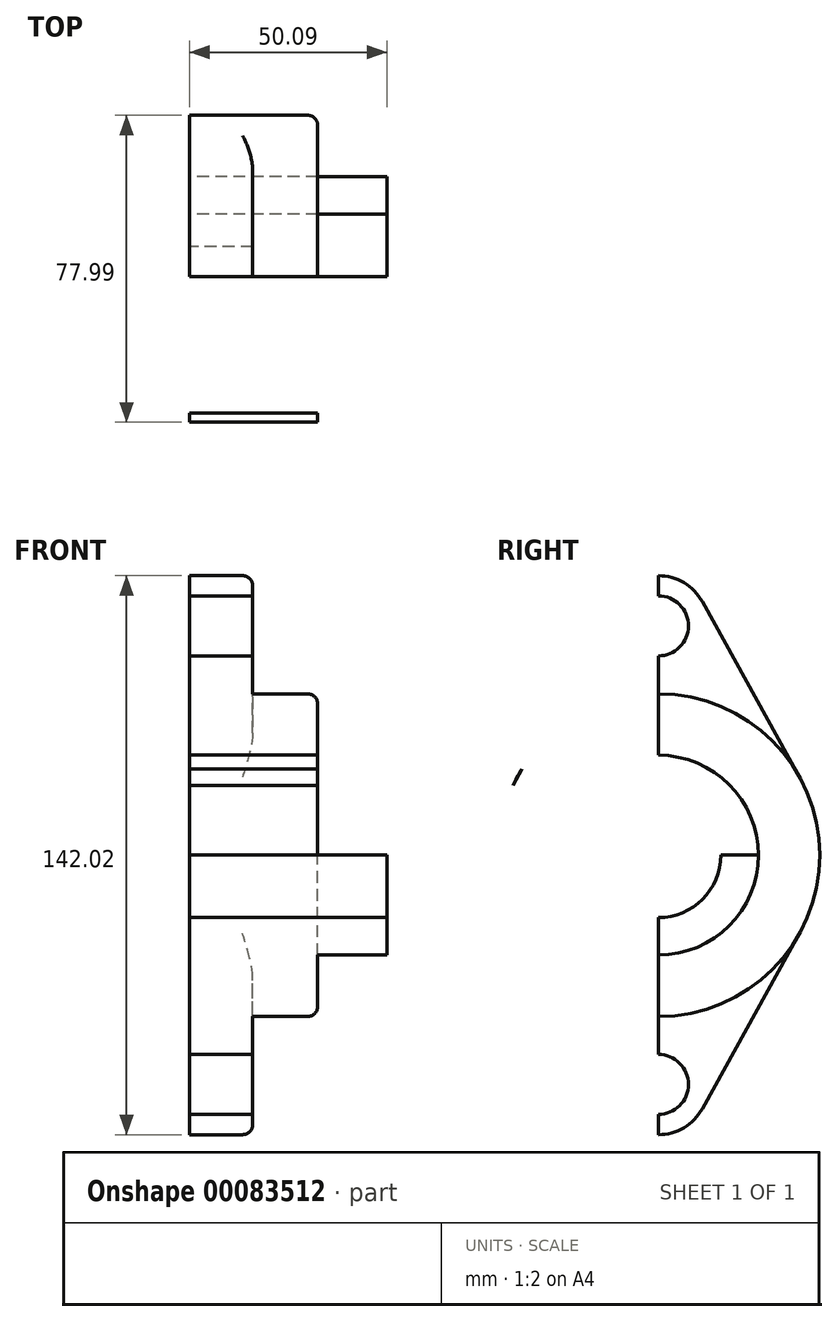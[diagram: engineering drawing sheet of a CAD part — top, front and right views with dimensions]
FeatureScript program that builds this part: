
annotation { "Feature Type Name" : "Feature", "Feature Type Description" : "" }
export const myFeature = defineFeature(function(context is Context, id is Id, definition is map)
    precondition{}
    {
        {
            var Q0;
            Q0=qCreatedBy(makeId("Right.planeOp"),FACE);
            var sketch = newSketch(context, id + "F0", { "sketchPlane" : qUnion([Q0])});
            skCircle(sketch, "E0", {"center": v(0, 0) * mm, "radius": 41 * mm});
            skLineSegment(sketch, "E1", {"start": v(0, 0) * mm, "end": v(0, 71) * mm});
            skLineSegment(sketch, "E2", {"start": v(0, 0) * mm, "end": v(0, 58.25) * mm});
            skCircle(sketch, "E3", {"center": v(0, 58.25) * mm, "radius": 7.62 * mm});
            skArc(sketch, "E4", {"start": v(11.17, 64.4) * mm, "mid": v(0.01, 71) * mm, "end": v(-11.16, 64.42) * mm});
            skCircle(sketch, "E5", {"center": v(0, 0) * mm, "radius": 15.88 * mm});
            skCircle(sketch, "E6", {"center": v(0, 0) * mm, "radius": 25.4 * mm});
            skLineSegment(sketch, "E7", {"start": v(-36.99, 17.68) * mm, "end": v(-11.16, 64.42) * mm});
            skLineSegment(sketch, "E8", {"start": v(11.17, 64.4) * mm, "end": v(35.85, 19.88) * mm});
            skLineSegment(sketch, "E9", {"start": v(0, 0) * mm, "end": v(31, 0) * mm});
            skLineSegment(sketch, "E10.MirrorCS", {"start": v(0, 0) * mm, "end": v(0, -71) * mm});
            skLineSegment(sketch, "E11.MirrorCS", {"start": v(0, 0) * mm, "end": v(0, -58.25) * mm});
            skCircle(sketch, "E12.MirrorC", {"center": v(0, -58.25) * mm, "radius": 7.62 * mm});
            skArc(sketch, "E13.MirrorC", {"start": v(11.17, -64.4) * mm, "mid": v(0.01, -71) * mm, "end": v(-11.16, -64.42) * mm});
            skLineSegment(sketch, "E14.MirrorCS", {"start": v(-36.99, -17.68) * mm, "end": v(-11.16, -64.42) * mm});
            skLineSegment(sketch, "E15.MirrorCS", {"start": v(11.17, -64.4) * mm, "end": v(35.85, -19.88) * mm});
            skSolve(sketch);
        }
        {
            var Q0;
            {var subQ5=sQuery(id+"F0.wireOp",EDGE,"E7");var subQ8=sQuery(id+"F0.wireOp",EDGE,"E0");var subQ9=makeQuery(id+"F0.imprint","INTERSECT",VERTEX,{"disambiguationData":[OD(1.0)],"derivedFrom":[subQ8,subQ5]});Q0=makeQuery(id+"F0.imprint","IMPRINT",FACE,{"disambiguationData":[TD([[makeQuery(id+"F0.imprint","IMPRINT",EDGE,{"disambiguationData":[TD([[subQ9,1.0]])],"derivedFrom":subQ8}),-1.0]])]});}
            var Q1;
            {var subQ8=sQuery(id+"F0.wireOp",EDGE,"E8");Q1=makeQuery(id+"F0.imprint","IMPRINT",FACE,{"disambiguationData":[TD([[makeQuery(id+"F0.imprint","IMPRINT",EDGE,{"derivedFrom":subQ8}),-1.0]])]});}
            var Q2;
            {var subQ7=sQuery(id+"F0.wireOp",EDGE,"E0");var subQ9=sQuery(id+"F0.wireOp",EDGE,"E14.MirrorCS");var subQ11=makeQuery(id+"F0.imprint","INTERSECT",VERTEX,{"disambiguationData":[OD(1.0)],"derivedFrom":[subQ7,subQ9]});Q2=makeQuery(id+"F0.imprint","IMPRINT",FACE,{"disambiguationData":[TD([[makeQuery(id+"F0.imprint","IMPRINT",EDGE,{"disambiguationData":[TD([[subQ11,-1.0]])],"derivedFrom":subQ7}),-1.0]])]});}
            var Q3;
            {var subQ7=sQuery(id+"F0.wireOp",EDGE,"E15.MirrorCS");Q3=makeQuery(id+"F0.imprint","IMPRINT",FACE,{"disambiguationData":[TD([[makeQuery(id+"F0.imprint","IMPRINT",EDGE,{"derivedFrom":subQ7}),1.0]])]});}
            extrude(context, id + "F1", {"entities" : qUnion([Q0, Q1, Q2, Q3]), "depth" : 16 * mm});
        }
        {
            var Q0;
            {var subQ1=sQuery(id+"F0.wireOp",EDGE,"E0");var subQ9=sQuery(id+"F0.wireOp",EDGE,"E7");var subQ12=makeQuery(id+"F0.imprint","INTERSECT",VERTEX,{"disambiguationData":[OD(1.0)],"derivedFrom":[subQ1,subQ9]});Q0=makeQuery(id+"F0.imprint","IMPRINT",FACE,{"disambiguationData":[TD([[makeQuery(id+"F0.imprint","IMPRINT",EDGE,{"disambiguationData":[TD([[subQ12,1.0]])],"derivedFrom":subQ1}),1.0]])]});}
            var Q1;
            {var subQ1=sQuery(id+"F0.wireOp",EDGE,"E0");var subQ5=makeQuery(id+"F0.imprint","INTERSECT",VERTEX,{"derivedFrom":[subQ1,sQuery(id+"F0.wireOp",EDGE,"E8")]});Q1=makeQuery(id+"F0.imprint","IMPRINT",FACE,{"disambiguationData":[TD([[makeQuery(id+"F0.imprint","IMPRINT",EDGE,{"disambiguationData":[TD([[subQ5,-1.0]])],"derivedFrom":subQ1}),1.0]])]});}
            extrude(context, id + "F2", {"entities" : qUnion([Q0, Q1]), "operationType" : NewBodyOperationType.ADD, "depth" : 32.5 * mm});
        }
        {
            var Q0;
            {var subQ0=sQuery(id+"F0.wireOp",EDGE,"E5");var subQ1=sQuery(id+"F0.wireOp",EDGE,"E2");var subQ2=makeQuery(id+"F0.imprint","INTERSECT",VERTEX,{"derivedFrom":[subQ1,subQ0]});Q0=makeQuery(id+"F0.imprint","IMPRINT",FACE,{"disambiguationData":[TD([[makeQuery(id+"F0.imprint","IMPRINT",EDGE,{"disambiguationData":[TD([[subQ2,-1.0]])],"derivedFrom":subQ1}),1.0]])]});}
            var Q1;
            {var subQ0=sQuery(id+"F0.wireOp",EDGE,"E5");var subQ1=sQuery(id+"F0.wireOp",EDGE,"E2");var subQ2=makeQuery(id+"F0.imprint","INTERSECT",VERTEX,{"derivedFrom":[subQ1,subQ0]});Q1=makeQuery(id+"F0.imprint","IMPRINT",FACE,{"disambiguationData":[TD([[makeQuery(id+"F0.imprint","IMPRINT",EDGE,{"disambiguationData":[TD([[subQ2,-1.0]])],"derivedFrom":subQ1}),-1.0]])]});}
            var Q2;
            {var subQ0=sQuery(id+"F0.wireOp",EDGE,"E9");var subQ1=sQuery(id+"F0.wireOp",EDGE,"E5");var subQ2=makeQuery(id+"F0.imprint","INTERSECT",VERTEX,{"derivedFrom":[subQ1,subQ0]});Q2=makeQuery(id+"F0.imprint","IMPRINT",FACE,{"disambiguationData":[TD([[makeQuery(id+"F0.imprint","IMPRINT",EDGE,{"disambiguationData":[TD([[subQ2,1.0]])],"derivedFrom":subQ1}),-1.0]])]});}
            extrude(context, id + "F3", {"entities" : qUnion([Q0, Q1, Q2]), "operationType" : NewBodyOperationType.ADD, "depth" : 50.1 * mm});
        }
        {
            var Q0;
            {var subQ0=sQuery(id+"F0.wireOp",EDGE,"E0");var subQ1=makeQuery(id+"F0.imprint","INTERSECT",VERTEX,{"derivedFrom":[subQ0,sQuery(id+"F0.wireOp",EDGE,"E8")]});var subQ2=makeQuery(id+"F0.imprint","INTERSECT",VERTEX,{"derivedFrom":[subQ0,sQuery(id+"F0.wireOp",EDGE,"E15.MirrorCS")]});Q0=makeQuery(id+"F2.opExtrude","CAP_EDGE",EDGE,{"disambiguationData":[OSD([subQ0]),TDD([makeQuery(id+"F0.imprint","IMPRINT",EDGE,{"disambiguationData":[TD([[subQ1,-1.0]])],"derivedFrom":subQ0}),makeQuery(id+"F0.imprint","IMPRINT",EDGE,{"disambiguationData":[TD([[makeQuery(id+"F0.imprint","INTERSECT",VERTEX,{"disambiguationData":[OD(1.0)],"derivedFrom":[subQ0,sQuery(id+"F0.wireOp",EDGE,"E7")]}),1.0]])],"derivedFrom":subQ0}),makeQuery(id+"F0.imprint","IMPRINT",EDGE,{"disambiguationData":[TD([[makeQuery(id+"F0.imprint","INTERSECT",VERTEX,{"disambiguationData":[OD(1.0)],"derivedFrom":[subQ0,sQuery(id+"F0.wireOp",EDGE,"E14.MirrorCS")]}),-1.0]])],"derivedFrom":subQ0}),makeQuery(id+"F0.imprint","IMPRINT",EDGE,{"disambiguationData":[TD([[subQ2,1.0]])],"derivedFrom":subQ0}),makeQuery(id+"F0.imprint","IMPRINT",EDGE,{"disambiguationData":[TD([[subQ1,1.0]])],"derivedFrom":subQ0})])],"isStart":false});}
            var Q1;
            Q1=makeQuery(id+"F1.opExtrude","CAP_EDGE",EDGE,{"disambiguationData":[OSD([sQuery(id+"F0.wireOp",EDGE,"E8")])],"isStart":false});
            var Q2;
            Q2=makeQuery(id+"F1.opExtrude","CAP_EDGE",EDGE,{"disambiguationData":[OSD([sQuery(id+"F0.wireOp",EDGE,"E4")])],"isStart":false});
            var Q3;
            Q3=makeQuery(id+"F1.opExtrude","CAP_EDGE",EDGE,{"disambiguationData":[OSD([sQuery(id+"F0.wireOp",EDGE,"E7")])],"isStart":false});
            var Q4;
            Q4=makeQuery(id+"F1.opExtrude","CAP_EDGE",EDGE,{"disambiguationData":[OSD([sQuery(id+"F0.wireOp",EDGE,"E14.MirrorCS")])],"isStart":false});
            var Q5;
            Q5=makeQuery(id+"F1.opExtrude","CAP_EDGE",EDGE,{"disambiguationData":[OSD([sQuery(id+"F0.wireOp",EDGE,"E13.MirrorC")])],"isStart":false});
            var Q6;
            Q6=makeQuery(id+"F1.opExtrude","CAP_EDGE",EDGE,{"disambiguationData":[OSD([sQuery(id+"F0.wireOp",EDGE,"E15.MirrorCS")])],"isStart":false});
            fillet(context, id + "F4", {"entities" : qUnion([Q0, Q1, Q2, Q3, Q4, Q5, Q6]), "radius" : 2.54 * mm, "tangentPropagation" : true, "allowEdgeOverflow" : false});
        }
    });
